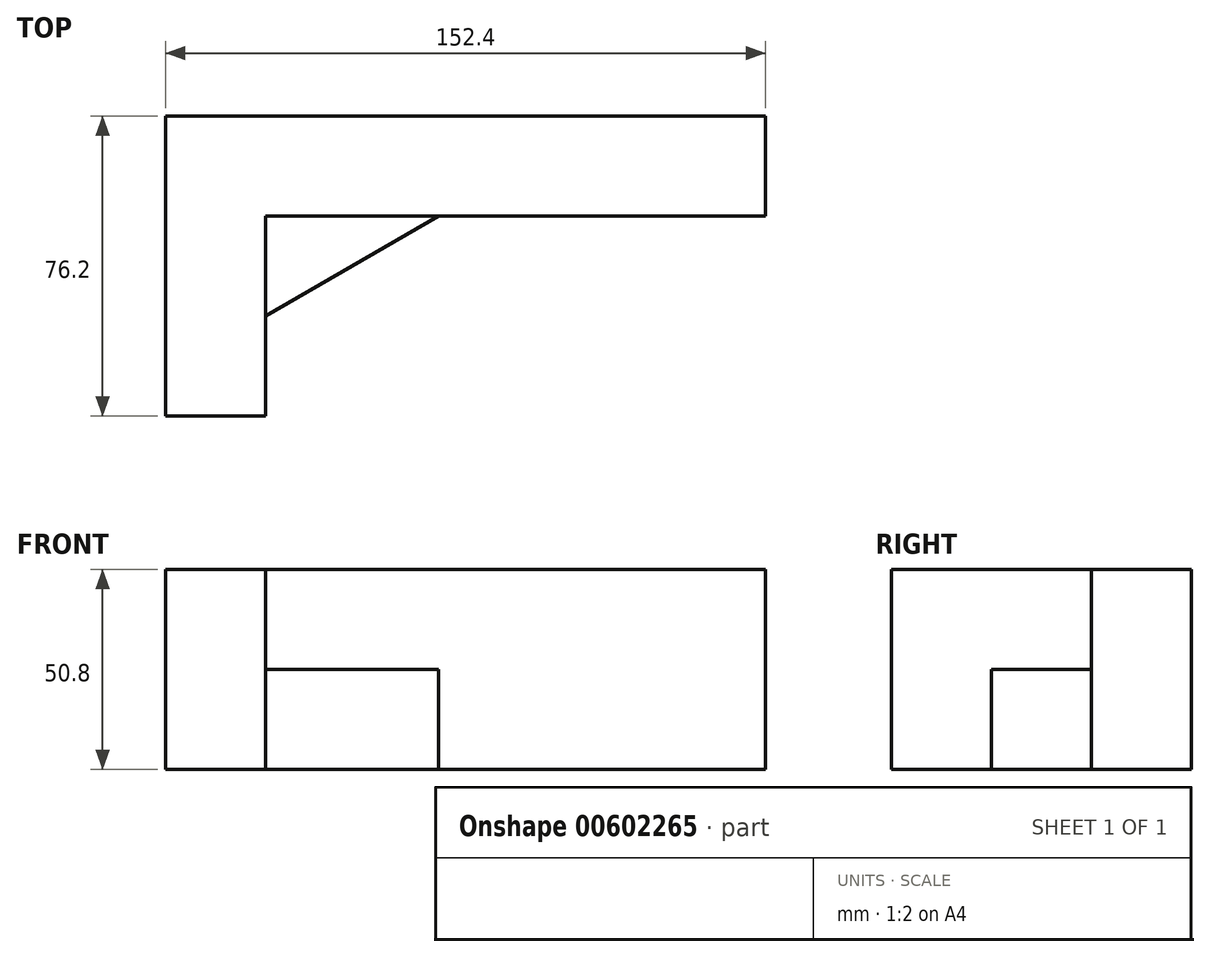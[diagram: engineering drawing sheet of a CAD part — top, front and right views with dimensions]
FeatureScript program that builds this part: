
annotation { "Feature Type Name" : "Feature", "Feature Type Description" : "" }
export const myFeature = defineFeature(function(context is Context, id is Id, definition is map)
    precondition{}
    {
        {
            var Q0;
            Q0=qCreatedBy(makeId("Top.planeOp"),FACE);
            var sketch = newSketch(context, id + "F0", { "sketchPlane" : qUnion([Q0])});
            skLineSegment(sketch, "E0", {"start": v(0, 0) * mm, "end": v(0, 76.2) * mm});
            skLineSegment(sketch, "E1", {"start": v(0, 76.2) * mm, "end": v(152.4, 76.2) * mm});
            skLineSegment(sketch, "E2", {"start": v(152.4, 76.2) * mm, "end": v(152.4, 50.8) * mm});
            skLineSegment(sketch, "E3", {"start": v(152.4, 50.8) * mm, "end": v(25.4, 50.8) * mm});
            skLineSegment(sketch, "E4", {"start": v(25.4, 50.8) * mm, "end": v(25.4, 0) * mm});
            skLineSegment(sketch, "E5", {"start": v(25.4, 0) * mm, "end": v(0, 0) * mm});
            skSolve(sketch);
        }
        {
            var Q0;
            Q0=makeQuery(id+"F0.imprint","IMPRINT",FACE,{"disambiguationData":[TD([[makeQuery(id+"F0.imprint","IMPRINT",EDGE,{"derivedFrom":sQuery(id+"F0.wireOp",EDGE,"E0")}),-1.0]])]});
            extrude(context, id + "F1", {"entities" : qUnion([Q0]), "oppositeDirection" : true, "depth" : 50.8 * mm, "offsetDistance" : 25.4 * mm});
        }
        {
            var Q0;
            Q0=makeQuery(id+"F1.opExtrude","CAP_FACE",FACE,{"disambiguationData":[OSD([sQuery(id+"F0.wireOp",EDGE,"E0"),sQuery(id+"F0.wireOp",EDGE,"E1"),sQuery(id+"F0.wireOp",EDGE,"E2"),sQuery(id+"F0.wireOp",EDGE,"E3"),sQuery(id+"F0.wireOp",EDGE,"E4"),sQuery(id+"F0.wireOp",EDGE,"E5")])],"isStart":false});
            var sketch = newSketch(context, id + "F2", { "sketchPlane" : qUnion([Q0])});
            skLineSegment(sketch, "E6", {"start": v(25.4, -25.4) * mm, "end": v(69.4, -50.8) * mm});
            skLineSegment(sketch, "E7", {"start": v(69.4, -50.8) * mm, "end": v(25.4, -50.8) * mm});
            skLineSegment(sketch, "E8", {"start": v(25.4, -50.8) * mm, "end": v(25.4, -25.4) * mm});
            skSolve(sketch);
        }
        {
            var Q0;
            Q0 = qSketchRegion(id + "F2", true);
            extrude(context, id + "F3", {"entities" : qUnion([Q0]), "oppositeDirection" : true, "depth" : 25.4 * mm, "offsetDistance" : 25.4 * mm});
        }
    });
